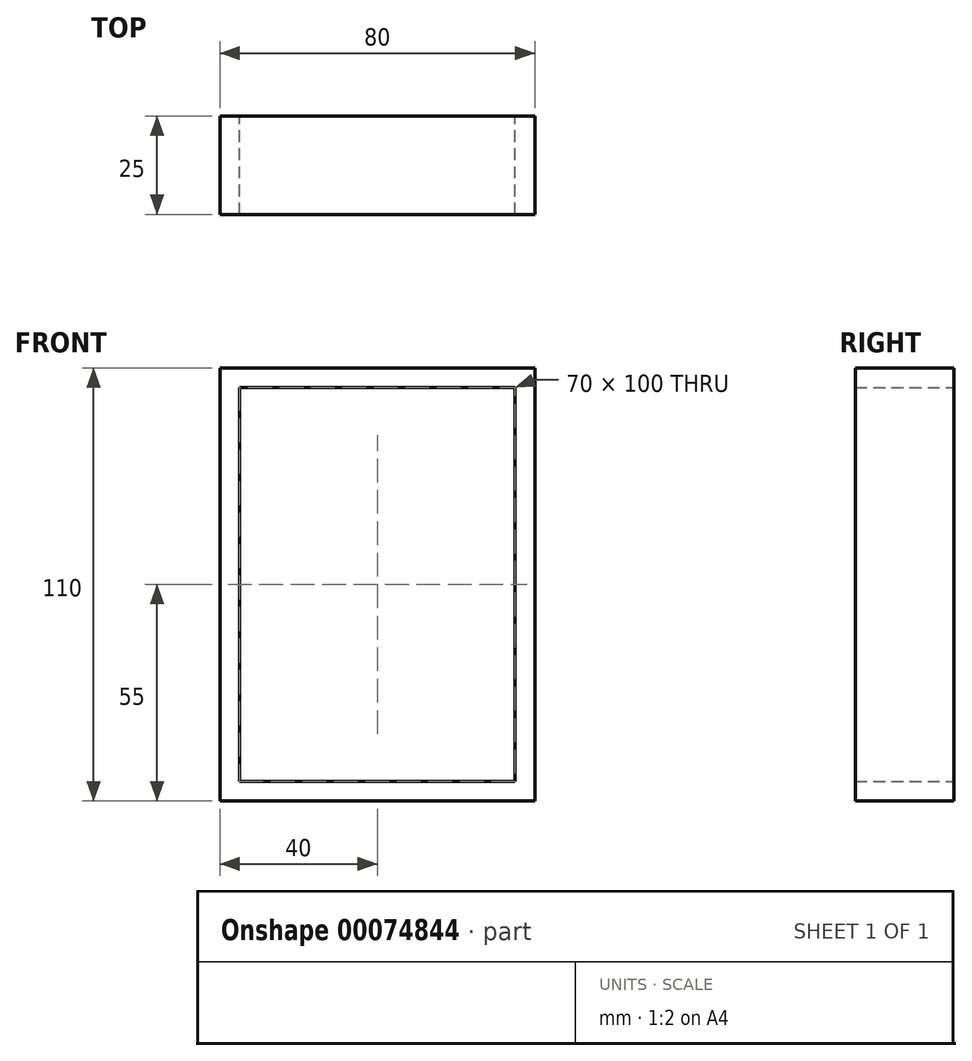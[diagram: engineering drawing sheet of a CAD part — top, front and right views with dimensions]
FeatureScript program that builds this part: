
annotation { "Feature Type Name" : "Feature", "Feature Type Description" : "" }
export const myFeature = defineFeature(function(context is Context, id is Id, definition is map)
    precondition{}
    {
        {
            var Q0;
            Q0=qCreatedBy(makeId("Front.planeOp"),FACE);
            var sketch = newSketch(context, id + "F0", { "sketchPlane" : qUnion([Q0])});
            skLineSegment(sketch, "E0.bottom", {"start": v(35, 50) * mm, "end": v(-35, 50) * mm});
            skLineSegment(sketch, "E0.top", {"start": v(35, -50) * mm, "end": v(-35, -50) * mm});
            skLineSegment(sketch, "E0.left", {"start": v(35, 50) * mm, "end": v(35, -50) * mm});
            skLineSegment(sketch, "E0.right", {"start": v(-35, 50) * mm, "end": v(-35, -50) * mm});
            skPoint(sketch, "E0.middle", {"position": v(0, 0) * mm});
            skLineSegment(sketch, "E1.0", {"start": v(40, 55) * mm, "end": v(-40, 55) * mm});
            skLineSegment(sketch, "E1.1", {"start": v(40, 55) * mm, "end": v(40, -55) * mm});
            skLineSegment(sketch, "E1.2", {"start": v(40, -55) * mm, "end": v(-40, -55) * mm});
            skLineSegment(sketch, "E1.3", {"start": v(-40, 55) * mm, "end": v(-40, -55) * mm});
            skSolve(sketch);
        }
        {
            var Q0;
            Q0=makeQuery(id+"F0.imprint","IMPRINT",FACE,{"disambiguationData":[TD([[makeQuery(id+"F0.imprint","IMPRINT",EDGE,{"derivedFrom":sQuery(id+"F0.wireOp",EDGE,"E0.bottom")}),-1.0]])]});
            extrude(context, id + "F1", {"entities" : qUnion([Q0]), "depth" : 25 * mm});
        }
    });
